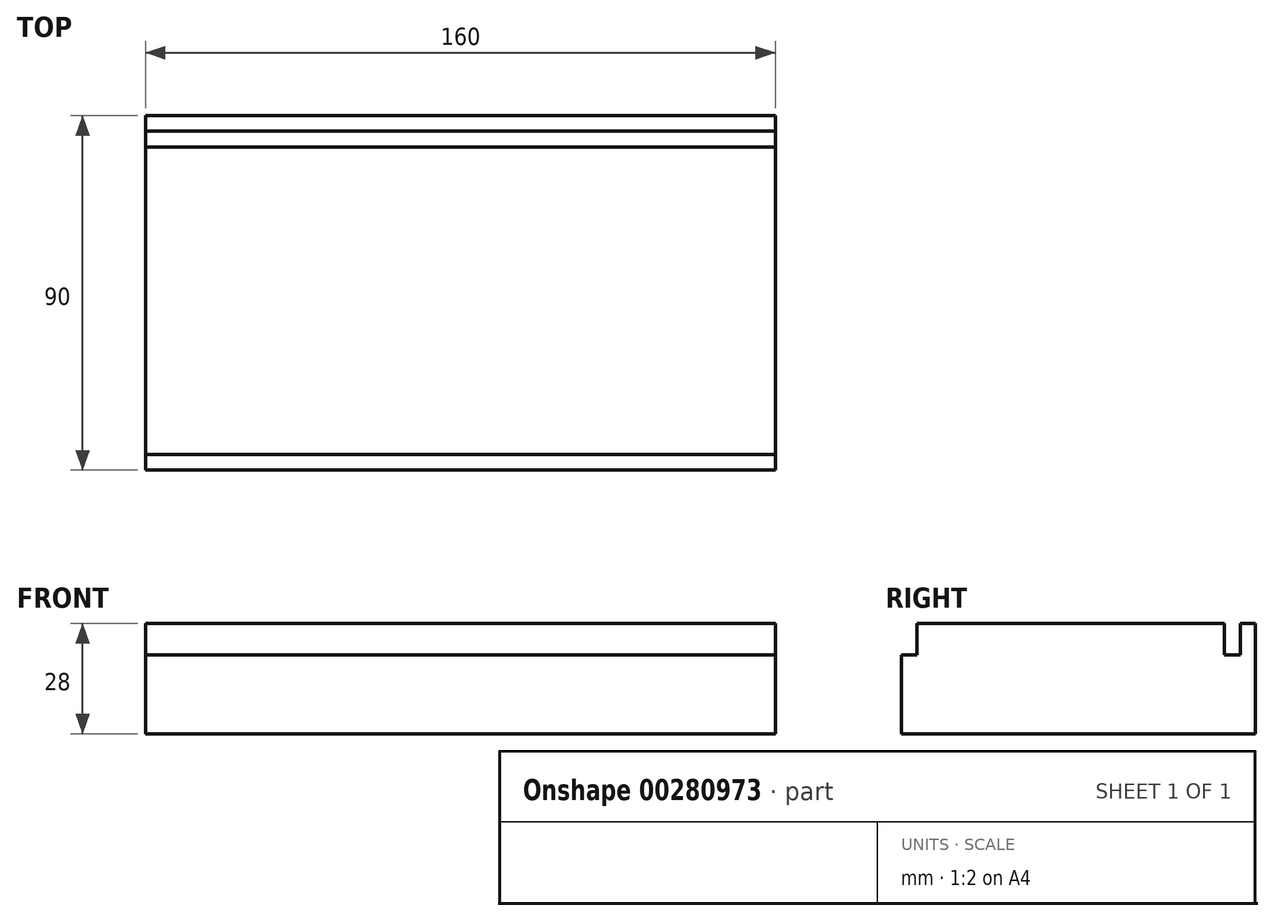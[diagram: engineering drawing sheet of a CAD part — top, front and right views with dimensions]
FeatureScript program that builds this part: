
annotation { "Feature Type Name" : "Feature", "Feature Type Description" : "" }
export const myFeature = defineFeature(function(context is Context, id is Id, definition is map)
    precondition{}
    {
        {
            var Q0;
            Q0=qCreatedBy(makeId("Right.planeOp"),FACE);
            var sketch = newSketch(context, id + "F0", { "sketchPlane" : qUnion([Q0])});
            skLineSegment(sketch, "E0", {"start": v(-45.14, 0) * mm, "end": v(-41.14, 0) * mm});
            skLineSegment(sketch, "E1", {"start": v(-41.14, 0) * mm, "end": v(-41.14, 8) * mm});
            skLineSegment(sketch, "E2", {"start": v(-41.14, 8) * mm, "end": v(36.95, 8) * mm});
            skLineSegment(sketch, "E3", {"start": v(36.95, 8) * mm, "end": v(36.95, 0) * mm});
            skLineSegment(sketch, "E4", {"start": v(36.95, 0) * mm, "end": v(40.95, 0) * mm});
            skLineSegment(sketch, "E5", {"start": v(40.95, 0) * mm, "end": v(40.95, 8) * mm});
            skLineSegment(sketch, "E6", {"start": v(40.95, 8) * mm, "end": v(44.86, 8) * mm});
            skLineSegment(sketch, "E7", {"start": v(44.86, 8) * mm, "end": v(44.86, -20) * mm});
            skLineSegment(sketch, "E8", {"start": v(44.86, -20) * mm, "end": v(-45.14, -20) * mm});
            skLineSegment(sketch, "E9", {"start": v(-45.14, -20) * mm, "end": v(-45.14, 0) * mm});
            skLineSegment(sketch, "E10", {"start": v(44.86, 0) * mm, "end": v(40.95, 0) * mm});
            skSolve(sketch);
        }
        {
            var Q0;
            Q0 = qSketchRegion(id + "F0", true);
            extrude(context, id + "F1", {"entities" : qUnion([Q0]), "depth" : 160 * mm});
        }
    });
